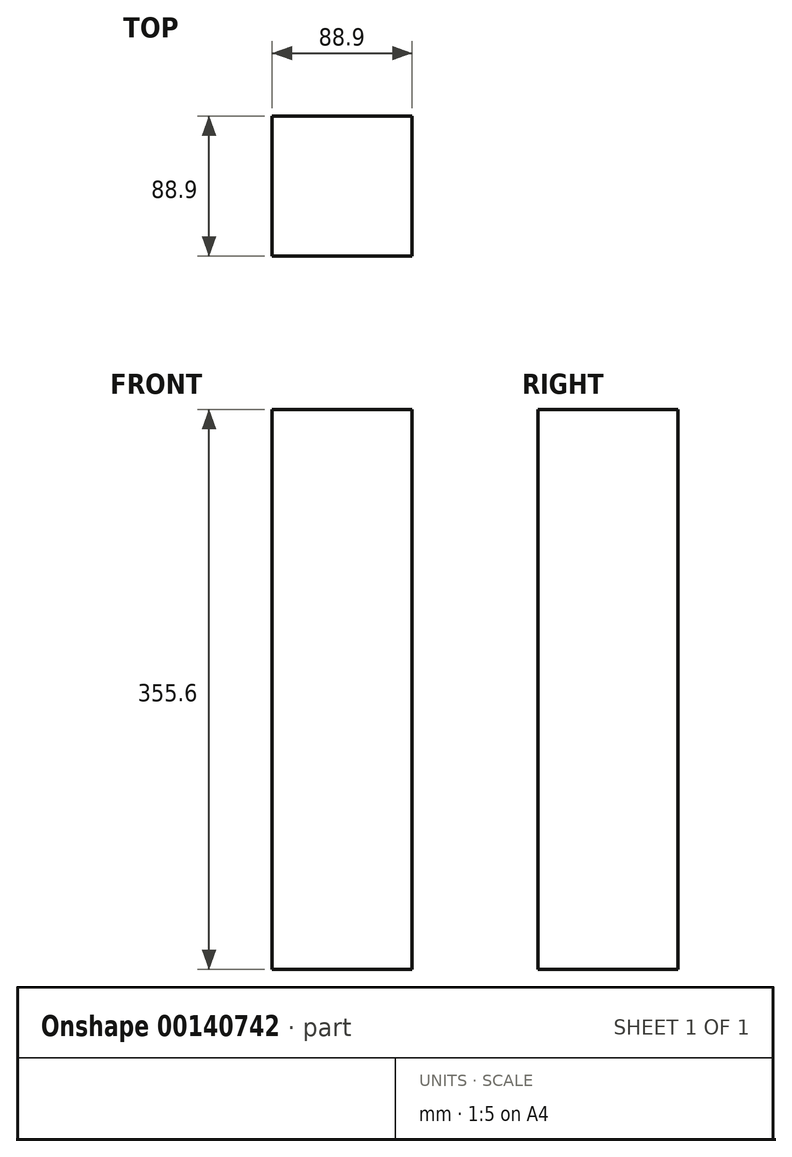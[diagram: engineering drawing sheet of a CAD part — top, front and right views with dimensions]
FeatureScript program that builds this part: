
annotation { "Feature Type Name" : "Feature", "Feature Type Description" : "" }
export const myFeature = defineFeature(function(context is Context, id is Id, definition is map)
    precondition{}
    {
        {
            var Q0;
            Q0=qCreatedBy(makeId("Top.planeOp"),FACE);
            var sketch = newSketch(context, id + "F0", { "sketchPlane" : qUnion([Q0])});
            skLineSegment(sketch, "E0.bottom", {"start": v(44.45, 44.45) * mm, "end": v(-44.45, 44.45) * mm});
            skLineSegment(sketch, "E0.top", {"start": v(44.45, -44.45) * mm, "end": v(-44.45, -44.45) * mm});
            skLineSegment(sketch, "E0.left", {"start": v(44.45, 44.45) * mm, "end": v(44.45, -44.45) * mm});
            skLineSegment(sketch, "E0.right", {"start": v(-44.45, 44.45) * mm, "end": v(-44.45, -44.45) * mm});
            skPoint(sketch, "E0.middle", {"position": v(0, 0) * mm});
            skSolve(sketch);
        }
        {
            var Q0;
            Q0=makeQuery(id+"F0.imprint","IMPRINT",FACE,{"disambiguationData":[TD([[makeQuery(id+"F0.imprint","IMPRINT",EDGE,{"derivedFrom":sQuery(id+"F0.wireOp",EDGE,"E0.bottom")}),1.0]])]});
            extrude(context, id + "F1", {"entities" : qUnion([Q0]), "depth" : 355.6 * mm});
        }
    });
